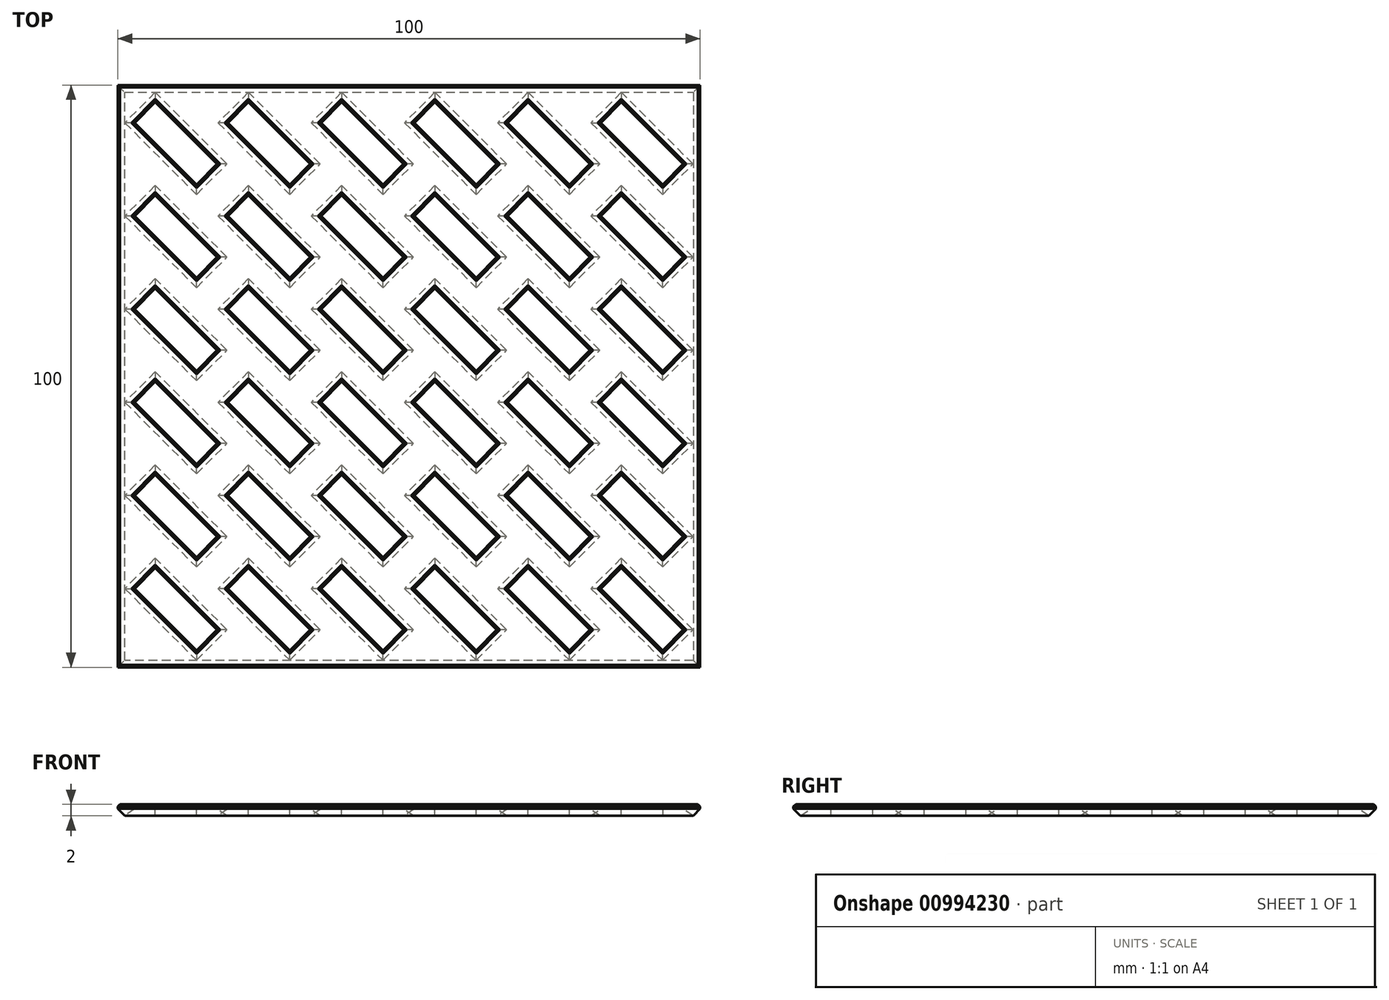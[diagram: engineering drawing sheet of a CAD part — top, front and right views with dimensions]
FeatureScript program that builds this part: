
annotation { "Feature Type Name" : "Feature", "Feature Type Description" : "" }
export const myFeature = defineFeature(function(context is Context, id is Id, definition is map)
    precondition{}
    {
        {
            var Q0;
            Q0=qCreatedBy(makeId("Top.planeOp"),FACE);
            var sketch = newSketch(context, id + "F0", { "sketchPlane" : qUnion([Q0])});
            skLineSegment(sketch, "E0.bottom", {"start": v(-50, -50) * mm, "end": v(50, -50) * mm});
            skLineSegment(sketch, "E0.top", {"start": v(-50, 50) * mm, "end": v(50, 50) * mm});
            skLineSegment(sketch, "E0.left", {"start": v(-50, -50) * mm, "end": v(-50, 50) * mm});
            skLineSegment(sketch, "E0.right", {"start": v(50, -50) * mm, "end": v(50, 50) * mm});
            skLineSegment(sketch, "E1", {"start": v(-50, 50) * mm, "end": v(50, -50) * mm, "construction": true});
            skLineSegment(sketch, "E2", {"start": v(-47.07, -36.46) * mm, "end": v(-36.46, -47.07) * mm});
            skLineSegment(sketch, "E3", {"start": v(-36.46, -47.07) * mm, "end": v(-32.93, -43.54) * mm});
            skLineSegment(sketch, "E4", {"start": v(-32.93, -43.54) * mm, "end": v(-43.54, -32.93) * mm});
            skLineSegment(sketch, "E5", {"start": v(-43.54, -32.93) * mm, "end": v(-47.07, -36.46) * mm});
            skLineSegment(sketch, "E6", {"start": v(-32.93, -43.54) * mm, "end": v(-40, -43.54) * mm, "construction": true});
            skLineSegment(sketch, "E7", {"start": v(-36.46, -47.07) * mm, "end": v(-36.46, -50) * mm, "construction": true});
            skLineSegment(sketch, "E8", {"start": v(-47.07, -36.46) * mm, "end": v(-50, -36.46) * mm, "construction": true});
            skLineSegment(sketch, "E9.0.1.0", {"start": v(-43.54, -16.93) * mm, "end": v(-47.07, -20.46) * mm});
            skLineSegment(sketch, "E9.0.1.1", {"start": v(-47.07, -20.46) * mm, "end": v(-36.46, -31.07) * mm});
            skLineSegment(sketch, "E9.0.1.2", {"start": v(-32.93, -27.54) * mm, "end": v(-43.54, -16.93) * mm});
            skLineSegment(sketch, "E9.0.1.3", {"start": v(-36.46, -31.07) * mm, "end": v(-32.93, -27.54) * mm});
            skLineSegment(sketch, "E9.0.2.0", {"start": v(-43.54, -0.93) * mm, "end": v(-47.07, -4.46) * mm});
            skLineSegment(sketch, "E9.0.2.1", {"start": v(-47.07, -4.46) * mm, "end": v(-36.46, -15.07) * mm});
            skLineSegment(sketch, "E9.0.2.2", {"start": v(-32.93, -11.54) * mm, "end": v(-43.54, -0.93) * mm});
            skLineSegment(sketch, "E9.0.2.3", {"start": v(-36.46, -15.07) * mm, "end": v(-32.93, -11.54) * mm});
            skLineSegment(sketch, "E9.0.3.0", {"start": v(-43.54, 15.07) * mm, "end": v(-47.07, 11.54) * mm});
            skLineSegment(sketch, "E9.0.3.1", {"start": v(-47.07, 11.54) * mm, "end": v(-36.46, 0.93) * mm});
            skLineSegment(sketch, "E9.0.3.2", {"start": v(-32.93, 4.46) * mm, "end": v(-43.54, 15.07) * mm});
            skLineSegment(sketch, "E9.0.3.3", {"start": v(-36.46, 0.93) * mm, "end": v(-32.93, 4.46) * mm});
            skLineSegment(sketch, "E9.0.4.0", {"start": v(-43.54, 31.07) * mm, "end": v(-47.07, 27.54) * mm});
            skLineSegment(sketch, "E9.0.4.1", {"start": v(-47.07, 27.54) * mm, "end": v(-36.46, 16.93) * mm});
            skLineSegment(sketch, "E9.0.4.2", {"start": v(-32.93, 20.46) * mm, "end": v(-43.54, 31.07) * mm});
            skLineSegment(sketch, "E9.0.4.3", {"start": v(-36.46, 16.93) * mm, "end": v(-32.93, 20.46) * mm});
            skLineSegment(sketch, "E9.0.5.0", {"start": v(-43.54, 47.07) * mm, "end": v(-47.07, 43.54) * mm});
            skLineSegment(sketch, "E9.0.5.1", {"start": v(-47.07, 43.54) * mm, "end": v(-36.46, 32.93) * mm});
            skLineSegment(sketch, "E9.0.5.2", {"start": v(-32.93, 36.46) * mm, "end": v(-43.54, 47.07) * mm});
            skLineSegment(sketch, "E9.0.5.3", {"start": v(-36.46, 32.93) * mm, "end": v(-32.93, 36.46) * mm});
            skLineSegment(sketch, "E9.1.0.0", {"start": v(-27.54, -32.93) * mm, "end": v(-31.07, -36.46) * mm});
            skLineSegment(sketch, "E9.1.0.1", {"start": v(-31.07, -36.46) * mm, "end": v(-20.46, -47.07) * mm});
            skLineSegment(sketch, "E9.1.0.2", {"start": v(-16.93, -43.54) * mm, "end": v(-27.54, -32.93) * mm});
            skLineSegment(sketch, "E9.1.0.3", {"start": v(-20.46, -47.07) * mm, "end": v(-16.93, -43.54) * mm});
            skLineSegment(sketch, "E9.1.1.0", {"start": v(-27.54, -16.93) * mm, "end": v(-31.07, -20.46) * mm});
            skLineSegment(sketch, "E9.1.1.1", {"start": v(-31.07, -20.46) * mm, "end": v(-20.46, -31.07) * mm});
            skLineSegment(sketch, "E9.1.1.2", {"start": v(-16.93, -27.54) * mm, "end": v(-27.54, -16.93) * mm});
            skLineSegment(sketch, "E9.1.1.3", {"start": v(-20.46, -31.07) * mm, "end": v(-16.93, -27.54) * mm});
            skLineSegment(sketch, "E9.1.2.0", {"start": v(-27.54, -0.93) * mm, "end": v(-31.07, -4.46) * mm});
            skLineSegment(sketch, "E9.1.2.1", {"start": v(-31.07, -4.46) * mm, "end": v(-20.46, -15.07) * mm});
            skLineSegment(sketch, "E9.1.2.2", {"start": v(-16.93, -11.54) * mm, "end": v(-27.54, -0.93) * mm});
            skLineSegment(sketch, "E9.1.2.3", {"start": v(-20.46, -15.07) * mm, "end": v(-16.93, -11.54) * mm});
            skLineSegment(sketch, "E9.1.3.0", {"start": v(-27.54, 15.07) * mm, "end": v(-31.07, 11.54) * mm});
            skLineSegment(sketch, "E9.1.3.1", {"start": v(-31.07, 11.54) * mm, "end": v(-20.46, 0.93) * mm});
            skLineSegment(sketch, "E9.1.3.2", {"start": v(-16.93, 4.46) * mm, "end": v(-27.54, 15.07) * mm});
            skLineSegment(sketch, "E9.1.3.3", {"start": v(-20.46, 0.93) * mm, "end": v(-16.93, 4.46) * mm});
            skLineSegment(sketch, "E9.1.4.0", {"start": v(-27.54, 31.07) * mm, "end": v(-31.07, 27.54) * mm});
            skLineSegment(sketch, "E9.1.4.1", {"start": v(-31.07, 27.54) * mm, "end": v(-20.46, 16.93) * mm});
            skLineSegment(sketch, "E9.1.4.2", {"start": v(-16.93, 20.46) * mm, "end": v(-27.54, 31.07) * mm});
            skLineSegment(sketch, "E9.1.4.3", {"start": v(-20.46, 16.93) * mm, "end": v(-16.93, 20.46) * mm});
            skLineSegment(sketch, "E9.1.5.0", {"start": v(-27.54, 47.07) * mm, "end": v(-31.07, 43.54) * mm});
            skLineSegment(sketch, "E9.1.5.1", {"start": v(-31.07, 43.54) * mm, "end": v(-20.46, 32.93) * mm});
            skLineSegment(sketch, "E9.1.5.2", {"start": v(-16.93, 36.46) * mm, "end": v(-27.54, 47.07) * mm});
            skLineSegment(sketch, "E9.1.5.3", {"start": v(-20.46, 32.93) * mm, "end": v(-16.93, 36.46) * mm});
            skLineSegment(sketch, "E9.2.0.0", {"start": v(-11.54, -32.93) * mm, "end": v(-15.07, -36.46) * mm});
            skLineSegment(sketch, "E9.2.0.1", {"start": v(-15.07, -36.46) * mm, "end": v(-4.46, -47.07) * mm});
            skLineSegment(sketch, "E9.2.0.2", {"start": v(-0.93, -43.54) * mm, "end": v(-11.54, -32.93) * mm});
            skLineSegment(sketch, "E9.2.0.3", {"start": v(-4.46, -47.07) * mm, "end": v(-0.93, -43.54) * mm});
            skLineSegment(sketch, "E9.2.1.0", {"start": v(-11.54, -16.93) * mm, "end": v(-15.07, -20.46) * mm});
            skLineSegment(sketch, "E9.2.1.1", {"start": v(-15.07, -20.46) * mm, "end": v(-4.46, -31.07) * mm});
            skLineSegment(sketch, "E9.2.1.2", {"start": v(-0.93, -27.54) * mm, "end": v(-11.54, -16.93) * mm});
            skLineSegment(sketch, "E9.2.1.3", {"start": v(-4.46, -31.07) * mm, "end": v(-0.93, -27.54) * mm});
            skLineSegment(sketch, "E9.2.2.0", {"start": v(-11.54, -0.93) * mm, "end": v(-15.07, -4.46) * mm});
            skLineSegment(sketch, "E9.2.2.1", {"start": v(-15.07, -4.46) * mm, "end": v(-4.46, -15.07) * mm});
            skLineSegment(sketch, "E9.2.2.2", {"start": v(-0.93, -11.54) * mm, "end": v(-11.54, -0.93) * mm});
            skLineSegment(sketch, "E9.2.2.3", {"start": v(-4.46, -15.07) * mm, "end": v(-0.93, -11.54) * mm});
            skLineSegment(sketch, "E9.2.3.0", {"start": v(-11.54, 15.07) * mm, "end": v(-15.07, 11.54) * mm});
            skLineSegment(sketch, "E9.2.3.1", {"start": v(-15.07, 11.54) * mm, "end": v(-4.46, 0.93) * mm});
            skLineSegment(sketch, "E9.2.3.2", {"start": v(-0.93, 4.46) * mm, "end": v(-11.54, 15.07) * mm});
            skLineSegment(sketch, "E9.2.3.3", {"start": v(-4.46, 0.93) * mm, "end": v(-0.93, 4.46) * mm});
            skLineSegment(sketch, "E9.2.4.0", {"start": v(-11.54, 31.07) * mm, "end": v(-15.07, 27.54) * mm});
            skLineSegment(sketch, "E9.2.4.1", {"start": v(-15.07, 27.54) * mm, "end": v(-4.46, 16.93) * mm});
            skLineSegment(sketch, "E9.2.4.2", {"start": v(-0.93, 20.46) * mm, "end": v(-11.54, 31.07) * mm});
            skLineSegment(sketch, "E9.2.4.3", {"start": v(-4.46, 16.93) * mm, "end": v(-0.93, 20.46) * mm});
            skLineSegment(sketch, "E9.2.5.0", {"start": v(-11.54, 47.07) * mm, "end": v(-15.07, 43.54) * mm});
            skLineSegment(sketch, "E9.2.5.1", {"start": v(-15.07, 43.54) * mm, "end": v(-4.46, 32.93) * mm});
            skLineSegment(sketch, "E9.2.5.2", {"start": v(-0.93, 36.46) * mm, "end": v(-11.54, 47.07) * mm});
            skLineSegment(sketch, "E9.2.5.3", {"start": v(-4.46, 32.93) * mm, "end": v(-0.93, 36.46) * mm});
            skLineSegment(sketch, "E9.3.0.0", {"start": v(4.46, -32.93) * mm, "end": v(0.93, -36.46) * mm});
            skLineSegment(sketch, "E9.3.0.1", {"start": v(0.93, -36.46) * mm, "end": v(11.54, -47.07) * mm});
            skLineSegment(sketch, "E9.3.0.2", {"start": v(15.07, -43.54) * mm, "end": v(4.46, -32.93) * mm});
            skLineSegment(sketch, "E9.3.0.3", {"start": v(11.54, -47.07) * mm, "end": v(15.07, -43.54) * mm});
            skLineSegment(sketch, "E9.3.1.0", {"start": v(4.46, -16.93) * mm, "end": v(0.93, -20.46) * mm});
            skLineSegment(sketch, "E9.3.1.1", {"start": v(0.93, -20.46) * mm, "end": v(11.54, -31.07) * mm});
            skLineSegment(sketch, "E9.3.1.2", {"start": v(15.07, -27.54) * mm, "end": v(4.46, -16.93) * mm});
            skLineSegment(sketch, "E9.3.1.3", {"start": v(11.54, -31.07) * mm, "end": v(15.07, -27.54) * mm});
            skLineSegment(sketch, "E9.3.2.0", {"start": v(4.46, -0.93) * mm, "end": v(0.93, -4.46) * mm});
            skLineSegment(sketch, "E9.3.2.1", {"start": v(0.93, -4.46) * mm, "end": v(11.54, -15.07) * mm});
            skLineSegment(sketch, "E9.3.2.2", {"start": v(15.07, -11.54) * mm, "end": v(4.46, -0.93) * mm});
            skLineSegment(sketch, "E9.3.2.3", {"start": v(11.54, -15.07) * mm, "end": v(15.07, -11.54) * mm});
            skLineSegment(sketch, "E9.3.3.0", {"start": v(4.46, 15.07) * mm, "end": v(0.93, 11.54) * mm});
            skLineSegment(sketch, "E9.3.3.1", {"start": v(0.93, 11.54) * mm, "end": v(11.54, 0.93) * mm});
            skLineSegment(sketch, "E9.3.3.2", {"start": v(15.07, 4.46) * mm, "end": v(4.46, 15.07) * mm});
            skLineSegment(sketch, "E9.3.3.3", {"start": v(11.54, 0.93) * mm, "end": v(15.07, 4.46) * mm});
            skLineSegment(sketch, "E9.3.4.0", {"start": v(4.46, 31.07) * mm, "end": v(0.93, 27.54) * mm});
            skLineSegment(sketch, "E9.3.4.1", {"start": v(0.93, 27.54) * mm, "end": v(11.54, 16.93) * mm});
            skLineSegment(sketch, "E9.3.4.2", {"start": v(15.07, 20.46) * mm, "end": v(4.46, 31.07) * mm});
            skLineSegment(sketch, "E9.3.4.3", {"start": v(11.54, 16.93) * mm, "end": v(15.07, 20.46) * mm});
            skLineSegment(sketch, "E9.3.5.0", {"start": v(4.46, 47.07) * mm, "end": v(0.93, 43.54) * mm});
            skLineSegment(sketch, "E9.3.5.1", {"start": v(0.93, 43.54) * mm, "end": v(11.54, 32.93) * mm});
            skLineSegment(sketch, "E9.3.5.2", {"start": v(15.07, 36.46) * mm, "end": v(4.46, 47.07) * mm});
            skLineSegment(sketch, "E9.3.5.3", {"start": v(11.54, 32.93) * mm, "end": v(15.07, 36.46) * mm});
            skLineSegment(sketch, "E9.4.0.0", {"start": v(20.46, -32.93) * mm, "end": v(16.93, -36.46) * mm});
            skLineSegment(sketch, "E9.4.0.1", {"start": v(16.93, -36.46) * mm, "end": v(27.54, -47.07) * mm});
            skLineSegment(sketch, "E9.4.0.2", {"start": v(31.07, -43.54) * mm, "end": v(20.46, -32.93) * mm});
            skLineSegment(sketch, "E9.4.0.3", {"start": v(27.54, -47.07) * mm, "end": v(31.07, -43.54) * mm});
            skLineSegment(sketch, "E9.4.1.0", {"start": v(20.46, -16.93) * mm, "end": v(16.93, -20.46) * mm});
            skLineSegment(sketch, "E9.4.1.1", {"start": v(16.93, -20.46) * mm, "end": v(27.54, -31.07) * mm});
            skLineSegment(sketch, "E9.4.1.2", {"start": v(31.07, -27.54) * mm, "end": v(20.46, -16.93) * mm});
            skLineSegment(sketch, "E9.4.1.3", {"start": v(27.54, -31.07) * mm, "end": v(31.07, -27.54) * mm});
            skLineSegment(sketch, "E9.4.2.0", {"start": v(20.46, -0.93) * mm, "end": v(16.93, -4.46) * mm});
            skLineSegment(sketch, "E9.4.2.1", {"start": v(16.93, -4.46) * mm, "end": v(27.54, -15.07) * mm});
            skLineSegment(sketch, "E9.4.2.2", {"start": v(31.07, -11.54) * mm, "end": v(20.46, -0.93) * mm});
            skLineSegment(sketch, "E9.4.2.3", {"start": v(27.54, -15.07) * mm, "end": v(31.07, -11.54) * mm});
            skLineSegment(sketch, "E9.4.3.0", {"start": v(20.46, 15.07) * mm, "end": v(16.93, 11.54) * mm});
            skLineSegment(sketch, "E9.4.3.1", {"start": v(16.93, 11.54) * mm, "end": v(27.54, 0.93) * mm});
            skLineSegment(sketch, "E9.4.3.2", {"start": v(31.07, 4.46) * mm, "end": v(20.46, 15.07) * mm});
            skLineSegment(sketch, "E9.4.3.3", {"start": v(27.54, 0.93) * mm, "end": v(31.07, 4.46) * mm});
            skLineSegment(sketch, "E9.4.4.0", {"start": v(20.46, 31.07) * mm, "end": v(16.93, 27.54) * mm});
            skLineSegment(sketch, "E9.4.4.1", {"start": v(16.93, 27.54) * mm, "end": v(27.54, 16.93) * mm});
            skLineSegment(sketch, "E9.4.4.2", {"start": v(31.07, 20.46) * mm, "end": v(20.46, 31.07) * mm});
            skLineSegment(sketch, "E9.4.4.3", {"start": v(27.54, 16.93) * mm, "end": v(31.07, 20.46) * mm});
            skLineSegment(sketch, "E9.4.5.0", {"start": v(20.46, 47.07) * mm, "end": v(16.93, 43.54) * mm});
            skLineSegment(sketch, "E9.4.5.1", {"start": v(16.93, 43.54) * mm, "end": v(27.54, 32.93) * mm});
            skLineSegment(sketch, "E9.4.5.2", {"start": v(31.07, 36.46) * mm, "end": v(20.46, 47.07) * mm});
            skLineSegment(sketch, "E9.4.5.3", {"start": v(27.54, 32.93) * mm, "end": v(31.07, 36.46) * mm});
            skLineSegment(sketch, "E9.5.0.0", {"start": v(36.46, -32.93) * mm, "end": v(32.93, -36.46) * mm});
            skLineSegment(sketch, "E9.5.0.1", {"start": v(32.93, -36.46) * mm, "end": v(43.54, -47.07) * mm});
            skLineSegment(sketch, "E9.5.0.2", {"start": v(47.07, -43.54) * mm, "end": v(36.46, -32.93) * mm});
            skLineSegment(sketch, "E9.5.0.3", {"start": v(43.54, -47.07) * mm, "end": v(47.07, -43.54) * mm});
            skLineSegment(sketch, "E9.5.1.0", {"start": v(36.46, -16.93) * mm, "end": v(32.93, -20.46) * mm});
            skLineSegment(sketch, "E9.5.1.1", {"start": v(32.93, -20.46) * mm, "end": v(43.54, -31.07) * mm});
            skLineSegment(sketch, "E9.5.1.2", {"start": v(47.07, -27.54) * mm, "end": v(36.46, -16.93) * mm});
            skLineSegment(sketch, "E9.5.1.3", {"start": v(43.54, -31.07) * mm, "end": v(47.07, -27.54) * mm});
            skLineSegment(sketch, "E9.5.2.0", {"start": v(36.46, -0.93) * mm, "end": v(32.93, -4.46) * mm});
            skLineSegment(sketch, "E9.5.2.1", {"start": v(32.93, -4.46) * mm, "end": v(43.54, -15.07) * mm});
            skLineSegment(sketch, "E9.5.2.2", {"start": v(47.07, -11.54) * mm, "end": v(36.46, -0.93) * mm});
            skLineSegment(sketch, "E9.5.2.3", {"start": v(43.54, -15.07) * mm, "end": v(47.07, -11.54) * mm});
            skLineSegment(sketch, "E9.5.3.0", {"start": v(36.46, 15.07) * mm, "end": v(32.93, 11.54) * mm});
            skLineSegment(sketch, "E9.5.3.1", {"start": v(32.93, 11.54) * mm, "end": v(43.54, 0.93) * mm});
            skLineSegment(sketch, "E9.5.3.2", {"start": v(47.07, 4.46) * mm, "end": v(36.46, 15.07) * mm});
            skLineSegment(sketch, "E9.5.3.3", {"start": v(43.54, 0.93) * mm, "end": v(47.07, 4.46) * mm});
            skLineSegment(sketch, "E9.5.4.0", {"start": v(36.46, 31.07) * mm, "end": v(32.93, 27.54) * mm});
            skLineSegment(sketch, "E9.5.4.1", {"start": v(32.93, 27.54) * mm, "end": v(43.54, 16.93) * mm});
            skLineSegment(sketch, "E9.5.4.2", {"start": v(47.07, 20.46) * mm, "end": v(36.46, 31.07) * mm});
            skLineSegment(sketch, "E9.5.4.3", {"start": v(43.54, 16.93) * mm, "end": v(47.07, 20.46) * mm});
            skLineSegment(sketch, "E9.5.5.0", {"start": v(36.46, 47.07) * mm, "end": v(32.93, 43.54) * mm});
            skLineSegment(sketch, "E9.5.5.1", {"start": v(32.93, 43.54) * mm, "end": v(43.54, 32.93) * mm});
            skLineSegment(sketch, "E9.5.5.2", {"start": v(47.07, 36.46) * mm, "end": v(36.46, 47.07) * mm});
            skLineSegment(sketch, "E9.5.5.3", {"start": v(43.54, 32.93) * mm, "end": v(47.07, 36.46) * mm});
            skLineSegment(sketch, "E9.direction1", {"start": v(-47.07, -36.46) * mm, "end": v(-31.07, -36.46) * mm, "construction": true});
            skLineSegment(sketch, "E9.direction2", {"start": v(-47.07, -36.46) * mm, "end": v(-47.07, -20.46) * mm, "construction": true});
            skLineSegment(sketch, "E10", {"start": v(36.46, 47.07) * mm, "end": v(36.46, 50) * mm, "construction": true});
            skLineSegment(sketch, "E11", {"start": v(47.07, 36.46) * mm, "end": v(50, 36.46) * mm, "construction": true});
            skSolve(sketch);
        }
        {
            var Q0;
            Q0=makeQuery(id+"F0.imprint","IMPRINT",FACE,{"disambiguationData":[TD([[makeQuery(id+"F0.imprint","IMPRINT",EDGE,{"derivedFrom":sQuery(id+"F0.wireOp",EDGE,"E0.bottom")}),1.0]])]});
            extrude(context, id + "F1", {"entities" : qUnion([Q0]), "depth" : 2 * mm, "offsetDistance" : 25 * mm});
        }
        {
            var Q0;
            Q0=makeQuery(id+"F1.opExtrude","CAP_FACE",FACE,{"disambiguationData":[OSD([sQuery(id+"F0.wireOp",EDGE,"E0.bottom"),sQuery(id+"F0.wireOp",EDGE,"E0.top"),sQuery(id+"F0.wireOp",EDGE,"E0.left"),sQuery(id+"F0.wireOp",EDGE,"E0.right"),sQuery(id+"F0.wireOp",EDGE,"E2"),sQuery(id+"F0.wireOp",EDGE,"E3"),sQuery(id+"F0.wireOp",EDGE,"E4"),sQuery(id+"F0.wireOp",EDGE,"E5"),sQuery(id+"F0.wireOp",EDGE,"E9.0.1.0"),sQuery(id+"F0.wireOp",EDGE,"E9.0.1.1"),sQuery(id+"F0.wireOp",EDGE,"E9.0.1.2"),sQuery(id+"F0.wireOp",EDGE,"E9.0.1.3"),sQuery(id+"F0.wireOp",EDGE,"E9.0.2.0"),sQuery(id+"F0.wireOp",EDGE,"E9.0.2.1"),sQuery(id+"F0.wireOp",EDGE,"E9.0.2.2"),sQuery(id+"F0.wireOp",EDGE,"E9.0.2.3"),sQuery(id+"F0.wireOp",EDGE,"E9.0.3.0"),sQuery(id+"F0.wireOp",EDGE,"E9.0.3.1"),sQuery(id+"F0.wireOp",EDGE,"E9.0.3.2"),sQuery(id+"F0.wireOp",EDGE,"E9.0.3.3"),sQuery(id+"F0.wireOp",EDGE,"E9.0.4.0"),sQuery(id+"F0.wireOp",EDGE,"E9.0.4.1"),sQuery(id+"F0.wireOp",EDGE,"E9.0.4.2"),sQuery(id+"F0.wireOp",EDGE,"E9.0.4.3"),sQuery(id+"F0.wireOp",EDGE,"E9.0.5.0"),sQuery(id+"F0.wireOp",EDGE,"E9.0.5.1"),sQuery(id+"F0.wireOp",EDGE,"E9.0.5.2"),sQuery(id+"F0.wireOp",EDGE,"E9.0.5.3"),sQuery(id+"F0.wireOp",EDGE,"E9.1.0.0"),sQuery(id+"F0.wireOp",EDGE,"E9.1.0.1"),sQuery(id+"F0.wireOp",EDGE,"E9.1.0.2"),sQuery(id+"F0.wireOp",EDGE,"E9.1.0.3"),sQuery(id+"F0.wireOp",EDGE,"E9.1.1.0"),sQuery(id+"F0.wireOp",EDGE,"E9.1.1.1"),sQuery(id+"F0.wireOp",EDGE,"E9.1.1.2"),sQuery(id+"F0.wireOp",EDGE,"E9.1.1.3"),sQuery(id+"F0.wireOp",EDGE,"E9.1.2.0"),sQuery(id+"F0.wireOp",EDGE,"E9.1.2.1"),sQuery(id+"F0.wireOp",EDGE,"E9.1.2.2"),sQuery(id+"F0.wireOp",EDGE,"E9.1.2.3"),sQuery(id+"F0.wireOp",EDGE,"E9.1.3.0"),sQuery(id+"F0.wireOp",EDGE,"E9.1.3.1"),sQuery(id+"F0.wireOp",EDGE,"E9.1.3.2"),sQuery(id+"F0.wireOp",EDGE,"E9.1.3.3"),sQuery(id+"F0.wireOp",EDGE,"E9.1.4.0"),sQuery(id+"F0.wireOp",EDGE,"E9.1.4.1"),sQuery(id+"F0.wireOp",EDGE,"E9.1.4.2"),sQuery(id+"F0.wireOp",EDGE,"E9.1.4.3"),sQuery(id+"F0.wireOp",EDGE,"E9.1.5.0"),sQuery(id+"F0.wireOp",EDGE,"E9.1.5.1"),sQuery(id+"F0.wireOp",EDGE,"E9.1.5.2"),sQuery(id+"F0.wireOp",EDGE,"E9.1.5.3"),sQuery(id+"F0.wireOp",EDGE,"E9.2.0.0"),sQuery(id+"F0.wireOp",EDGE,"E9.2.0.1"),sQuery(id+"F0.wireOp",EDGE,"E9.2.0.2"),sQuery(id+"F0.wireOp",EDGE,"E9.2.0.3"),sQuery(id+"F0.wireOp",EDGE,"E9.2.1.0"),sQuery(id+"F0.wireOp",EDGE,"E9.2.1.1"),sQuery(id+"F0.wireOp",EDGE,"E9.2.1.2"),sQuery(id+"F0.wireOp",EDGE,"E9.2.1.3"),sQuery(id+"F0.wireOp",EDGE,"E9.2.2.0"),sQuery(id+"F0.wireOp",EDGE,"E9.2.2.1"),sQuery(id+"F0.wireOp",EDGE,"E9.2.2.2"),sQuery(id+"F0.wireOp",EDGE,"E9.2.2.3"),sQuery(id+"F0.wireOp",EDGE,"E9.2.3.0"),sQuery(id+"F0.wireOp",EDGE,"E9.2.3.1"),sQuery(id+"F0.wireOp",EDGE,"E9.2.3.2"),sQuery(id+"F0.wireOp",EDGE,"E9.2.3.3"),sQuery(id+"F0.wireOp",EDGE,"E9.2.4.0"),sQuery(id+"F0.wireOp",EDGE,"E9.2.4.1"),sQuery(id+"F0.wireOp",EDGE,"E9.2.4.2"),sQuery(id+"F0.wireOp",EDGE,"E9.2.4.3"),sQuery(id+"F0.wireOp",EDGE,"E9.2.5.0"),sQuery(id+"F0.wireOp",EDGE,"E9.2.5.1"),sQuery(id+"F0.wireOp",EDGE,"E9.2.5.2"),sQuery(id+"F0.wireOp",EDGE,"E9.2.5.3"),sQuery(id+"F0.wireOp",EDGE,"E9.3.0.0"),sQuery(id+"F0.wireOp",EDGE,"E9.3.0.1"),sQuery(id+"F0.wireOp",EDGE,"E9.3.0.2"),sQuery(id+"F0.wireOp",EDGE,"E9.3.0.3"),sQuery(id+"F0.wireOp",EDGE,"E9.3.1.0"),sQuery(id+"F0.wireOp",EDGE,"E9.3.1.1"),sQuery(id+"F0.wireOp",EDGE,"E9.3.1.2"),sQuery(id+"F0.wireOp",EDGE,"E9.3.1.3"),sQuery(id+"F0.wireOp",EDGE,"E9.3.2.0"),sQuery(id+"F0.wireOp",EDGE,"E9.3.2.1"),sQuery(id+"F0.wireOp",EDGE,"E9.3.2.2"),sQuery(id+"F0.wireOp",EDGE,"E9.3.2.3"),sQuery(id+"F0.wireOp",EDGE,"E9.3.3.0"),sQuery(id+"F0.wireOp",EDGE,"E9.3.3.1"),sQuery(id+"F0.wireOp",EDGE,"E9.3.3.2"),sQuery(id+"F0.wireOp",EDGE,"E9.3.3.3"),sQuery(id+"F0.wireOp",EDGE,"E9.3.4.0"),sQuery(id+"F0.wireOp",EDGE,"E9.3.4.1"),sQuery(id+"F0.wireOp",EDGE,"E9.3.4.2"),sQuery(id+"F0.wireOp",EDGE,"E9.3.4.3"),sQuery(id+"F0.wireOp",EDGE,"E9.3.5.0"),sQuery(id+"F0.wireOp",EDGE,"E9.3.5.1"),sQuery(id+"F0.wireOp",EDGE,"E9.3.5.2"),sQuery(id+"F0.wireOp",EDGE,"E9.3.5.3"),sQuery(id+"F0.wireOp",EDGE,"E9.4.0.0"),sQuery(id+"F0.wireOp",EDGE,"E9.4.0.1"),sQuery(id+"F0.wireOp",EDGE,"E9.4.0.2"),sQuery(id+"F0.wireOp",EDGE,"E9.4.0.3"),sQuery(id+"F0.wireOp",EDGE,"E9.4.1.0"),sQuery(id+"F0.wireOp",EDGE,"E9.4.1.1"),sQuery(id+"F0.wireOp",EDGE,"E9.4.1.2"),sQuery(id+"F0.wireOp",EDGE,"E9.4.1.3"),sQuery(id+"F0.wireOp",EDGE,"E9.4.2.0"),sQuery(id+"F0.wireOp",EDGE,"E9.4.2.1"),sQuery(id+"F0.wireOp",EDGE,"E9.4.2.2"),sQuery(id+"F0.wireOp",EDGE,"E9.4.2.3"),sQuery(id+"F0.wireOp",EDGE,"E9.4.3.0"),sQuery(id+"F0.wireOp",EDGE,"E9.4.3.1"),sQuery(id+"F0.wireOp",EDGE,"E9.4.3.2"),sQuery(id+"F0.wireOp",EDGE,"E9.4.3.3"),sQuery(id+"F0.wireOp",EDGE,"E9.4.4.0"),sQuery(id+"F0.wireOp",EDGE,"E9.4.4.1"),sQuery(id+"F0.wireOp",EDGE,"E9.4.4.2"),sQuery(id+"F0.wireOp",EDGE,"E9.4.4.3"),sQuery(id+"F0.wireOp",EDGE,"E9.4.5.0"),sQuery(id+"F0.wireOp",EDGE,"E9.4.5.1"),sQuery(id+"F0.wireOp",EDGE,"E9.4.5.2"),sQuery(id+"F0.wireOp",EDGE,"E9.4.5.3"),sQuery(id+"F0.wireOp",EDGE,"E9.5.0.0"),sQuery(id+"F0.wireOp",EDGE,"E9.5.0.1"),sQuery(id+"F0.wireOp",EDGE,"E9.5.0.2"),sQuery(id+"F0.wireOp",EDGE,"E9.5.0.3"),sQuery(id+"F0.wireOp",EDGE,"E9.5.1.0"),sQuery(id+"F0.wireOp",EDGE,"E9.5.1.1"),sQuery(id+"F0.wireOp",EDGE,"E9.5.1.2"),sQuery(id+"F0.wireOp",EDGE,"E9.5.1.3"),sQuery(id+"F0.wireOp",EDGE,"E9.5.2.0"),sQuery(id+"F0.wireOp",EDGE,"E9.5.2.1"),sQuery(id+"F0.wireOp",EDGE,"E9.5.2.2"),sQuery(id+"F0.wireOp",EDGE,"E9.5.2.3"),sQuery(id+"F0.wireOp",EDGE,"E9.5.3.0"),sQuery(id+"F0.wireOp",EDGE,"E9.5.3.1"),sQuery(id+"F0.wireOp",EDGE,"E9.5.3.2"),sQuery(id+"F0.wireOp",EDGE,"E9.5.3.3"),sQuery(id+"F0.wireOp",EDGE,"E9.5.4.0"),sQuery(id+"F0.wireOp",EDGE,"E9.5.4.1"),sQuery(id+"F0.wireOp",EDGE,"E9.5.4.2"),sQuery(id+"F0.wireOp",EDGE,"E9.5.4.3"),sQuery(id+"F0.wireOp",EDGE,"E9.5.5.0"),sQuery(id+"F0.wireOp",EDGE,"E9.5.5.1"),sQuery(id+"F0.wireOp",EDGE,"E9.5.5.2"),sQuery(id+"F0.wireOp",EDGE,"E9.5.5.3")])],"isStart":false});
            chamfer(context, id + "F2", {"entities" : qUnion([Q0]), "width" : .4 * mm, "tangentPropagation" : true});
        }
        {
            var Q0;
            Q0=makeQuery(id+"F1.opExtrude","CAP_FACE",FACE,{"disambiguationData":[OSD([sQuery(id+"F0.wireOp",EDGE,"E0.bottom"),sQuery(id+"F0.wireOp",EDGE,"E0.top"),sQuery(id+"F0.wireOp",EDGE,"E0.left"),sQuery(id+"F0.wireOp",EDGE,"E0.right"),sQuery(id+"F0.wireOp",EDGE,"E2"),sQuery(id+"F0.wireOp",EDGE,"E3"),sQuery(id+"F0.wireOp",EDGE,"E4"),sQuery(id+"F0.wireOp",EDGE,"E5"),sQuery(id+"F0.wireOp",EDGE,"E9.0.1.0"),sQuery(id+"F0.wireOp",EDGE,"E9.0.1.1"),sQuery(id+"F0.wireOp",EDGE,"E9.0.1.2"),sQuery(id+"F0.wireOp",EDGE,"E9.0.1.3"),sQuery(id+"F0.wireOp",EDGE,"E9.0.2.0"),sQuery(id+"F0.wireOp",EDGE,"E9.0.2.1"),sQuery(id+"F0.wireOp",EDGE,"E9.0.2.2"),sQuery(id+"F0.wireOp",EDGE,"E9.0.2.3"),sQuery(id+"F0.wireOp",EDGE,"E9.0.3.0"),sQuery(id+"F0.wireOp",EDGE,"E9.0.3.1"),sQuery(id+"F0.wireOp",EDGE,"E9.0.3.2"),sQuery(id+"F0.wireOp",EDGE,"E9.0.3.3"),sQuery(id+"F0.wireOp",EDGE,"E9.0.4.0"),sQuery(id+"F0.wireOp",EDGE,"E9.0.4.1"),sQuery(id+"F0.wireOp",EDGE,"E9.0.4.2"),sQuery(id+"F0.wireOp",EDGE,"E9.0.4.3"),sQuery(id+"F0.wireOp",EDGE,"E9.0.5.0"),sQuery(id+"F0.wireOp",EDGE,"E9.0.5.1"),sQuery(id+"F0.wireOp",EDGE,"E9.0.5.2"),sQuery(id+"F0.wireOp",EDGE,"E9.0.5.3"),sQuery(id+"F0.wireOp",EDGE,"E9.1.0.0"),sQuery(id+"F0.wireOp",EDGE,"E9.1.0.1"),sQuery(id+"F0.wireOp",EDGE,"E9.1.0.2"),sQuery(id+"F0.wireOp",EDGE,"E9.1.0.3"),sQuery(id+"F0.wireOp",EDGE,"E9.1.1.0"),sQuery(id+"F0.wireOp",EDGE,"E9.1.1.1"),sQuery(id+"F0.wireOp",EDGE,"E9.1.1.2"),sQuery(id+"F0.wireOp",EDGE,"E9.1.1.3"),sQuery(id+"F0.wireOp",EDGE,"E9.1.2.0"),sQuery(id+"F0.wireOp",EDGE,"E9.1.2.1"),sQuery(id+"F0.wireOp",EDGE,"E9.1.2.2"),sQuery(id+"F0.wireOp",EDGE,"E9.1.2.3"),sQuery(id+"F0.wireOp",EDGE,"E9.1.3.0"),sQuery(id+"F0.wireOp",EDGE,"E9.1.3.1"),sQuery(id+"F0.wireOp",EDGE,"E9.1.3.2"),sQuery(id+"F0.wireOp",EDGE,"E9.1.3.3"),sQuery(id+"F0.wireOp",EDGE,"E9.1.4.0"),sQuery(id+"F0.wireOp",EDGE,"E9.1.4.1"),sQuery(id+"F0.wireOp",EDGE,"E9.1.4.2"),sQuery(id+"F0.wireOp",EDGE,"E9.1.4.3"),sQuery(id+"F0.wireOp",EDGE,"E9.1.5.0"),sQuery(id+"F0.wireOp",EDGE,"E9.1.5.1"),sQuery(id+"F0.wireOp",EDGE,"E9.1.5.2"),sQuery(id+"F0.wireOp",EDGE,"E9.1.5.3"),sQuery(id+"F0.wireOp",EDGE,"E9.2.0.0"),sQuery(id+"F0.wireOp",EDGE,"E9.2.0.1"),sQuery(id+"F0.wireOp",EDGE,"E9.2.0.2"),sQuery(id+"F0.wireOp",EDGE,"E9.2.0.3"),sQuery(id+"F0.wireOp",EDGE,"E9.2.1.0"),sQuery(id+"F0.wireOp",EDGE,"E9.2.1.1"),sQuery(id+"F0.wireOp",EDGE,"E9.2.1.2"),sQuery(id+"F0.wireOp",EDGE,"E9.2.1.3"),sQuery(id+"F0.wireOp",EDGE,"E9.2.2.0"),sQuery(id+"F0.wireOp",EDGE,"E9.2.2.1"),sQuery(id+"F0.wireOp",EDGE,"E9.2.2.2"),sQuery(id+"F0.wireOp",EDGE,"E9.2.2.3"),sQuery(id+"F0.wireOp",EDGE,"E9.2.3.0"),sQuery(id+"F0.wireOp",EDGE,"E9.2.3.1"),sQuery(id+"F0.wireOp",EDGE,"E9.2.3.2"),sQuery(id+"F0.wireOp",EDGE,"E9.2.3.3"),sQuery(id+"F0.wireOp",EDGE,"E9.2.4.0"),sQuery(id+"F0.wireOp",EDGE,"E9.2.4.1"),sQuery(id+"F0.wireOp",EDGE,"E9.2.4.2"),sQuery(id+"F0.wireOp",EDGE,"E9.2.4.3"),sQuery(id+"F0.wireOp",EDGE,"E9.2.5.0"),sQuery(id+"F0.wireOp",EDGE,"E9.2.5.1"),sQuery(id+"F0.wireOp",EDGE,"E9.2.5.2"),sQuery(id+"F0.wireOp",EDGE,"E9.2.5.3"),sQuery(id+"F0.wireOp",EDGE,"E9.3.0.0"),sQuery(id+"F0.wireOp",EDGE,"E9.3.0.1"),sQuery(id+"F0.wireOp",EDGE,"E9.3.0.2"),sQuery(id+"F0.wireOp",EDGE,"E9.3.0.3"),sQuery(id+"F0.wireOp",EDGE,"E9.3.1.0"),sQuery(id+"F0.wireOp",EDGE,"E9.3.1.1"),sQuery(id+"F0.wireOp",EDGE,"E9.3.1.2"),sQuery(id+"F0.wireOp",EDGE,"E9.3.1.3"),sQuery(id+"F0.wireOp",EDGE,"E9.3.2.0"),sQuery(id+"F0.wireOp",EDGE,"E9.3.2.1"),sQuery(id+"F0.wireOp",EDGE,"E9.3.2.2"),sQuery(id+"F0.wireOp",EDGE,"E9.3.2.3"),sQuery(id+"F0.wireOp",EDGE,"E9.3.3.0"),sQuery(id+"F0.wireOp",EDGE,"E9.3.3.1"),sQuery(id+"F0.wireOp",EDGE,"E9.3.3.2"),sQuery(id+"F0.wireOp",EDGE,"E9.3.3.3"),sQuery(id+"F0.wireOp",EDGE,"E9.3.4.0"),sQuery(id+"F0.wireOp",EDGE,"E9.3.4.1"),sQuery(id+"F0.wireOp",EDGE,"E9.3.4.2"),sQuery(id+"F0.wireOp",EDGE,"E9.3.4.3"),sQuery(id+"F0.wireOp",EDGE,"E9.3.5.0"),sQuery(id+"F0.wireOp",EDGE,"E9.3.5.1"),sQuery(id+"F0.wireOp",EDGE,"E9.3.5.2"),sQuery(id+"F0.wireOp",EDGE,"E9.3.5.3"),sQuery(id+"F0.wireOp",EDGE,"E9.4.0.0"),sQuery(id+"F0.wireOp",EDGE,"E9.4.0.1"),sQuery(id+"F0.wireOp",EDGE,"E9.4.0.2"),sQuery(id+"F0.wireOp",EDGE,"E9.4.0.3"),sQuery(id+"F0.wireOp",EDGE,"E9.4.1.0"),sQuery(id+"F0.wireOp",EDGE,"E9.4.1.1"),sQuery(id+"F0.wireOp",EDGE,"E9.4.1.2"),sQuery(id+"F0.wireOp",EDGE,"E9.4.1.3"),sQuery(id+"F0.wireOp",EDGE,"E9.4.2.0"),sQuery(id+"F0.wireOp",EDGE,"E9.4.2.1"),sQuery(id+"F0.wireOp",EDGE,"E9.4.2.2"),sQuery(id+"F0.wireOp",EDGE,"E9.4.2.3"),sQuery(id+"F0.wireOp",EDGE,"E9.4.3.0"),sQuery(id+"F0.wireOp",EDGE,"E9.4.3.1"),sQuery(id+"F0.wireOp",EDGE,"E9.4.3.2"),sQuery(id+"F0.wireOp",EDGE,"E9.4.3.3"),sQuery(id+"F0.wireOp",EDGE,"E9.4.4.0"),sQuery(id+"F0.wireOp",EDGE,"E9.4.4.1"),sQuery(id+"F0.wireOp",EDGE,"E9.4.4.2"),sQuery(id+"F0.wireOp",EDGE,"E9.4.4.3"),sQuery(id+"F0.wireOp",EDGE,"E9.4.5.0"),sQuery(id+"F0.wireOp",EDGE,"E9.4.5.1"),sQuery(id+"F0.wireOp",EDGE,"E9.4.5.2"),sQuery(id+"F0.wireOp",EDGE,"E9.4.5.3"),sQuery(id+"F0.wireOp",EDGE,"E9.5.0.0"),sQuery(id+"F0.wireOp",EDGE,"E9.5.0.1"),sQuery(id+"F0.wireOp",EDGE,"E9.5.0.2"),sQuery(id+"F0.wireOp",EDGE,"E9.5.0.3"),sQuery(id+"F0.wireOp",EDGE,"E9.5.1.0"),sQuery(id+"F0.wireOp",EDGE,"E9.5.1.1"),sQuery(id+"F0.wireOp",EDGE,"E9.5.1.2"),sQuery(id+"F0.wireOp",EDGE,"E9.5.1.3"),sQuery(id+"F0.wireOp",EDGE,"E9.5.2.0"),sQuery(id+"F0.wireOp",EDGE,"E9.5.2.1"),sQuery(id+"F0.wireOp",EDGE,"E9.5.2.2"),sQuery(id+"F0.wireOp",EDGE,"E9.5.2.3"),sQuery(id+"F0.wireOp",EDGE,"E9.5.3.0"),sQuery(id+"F0.wireOp",EDGE,"E9.5.3.1"),sQuery(id+"F0.wireOp",EDGE,"E9.5.3.2"),sQuery(id+"F0.wireOp",EDGE,"E9.5.3.3"),sQuery(id+"F0.wireOp",EDGE,"E9.5.4.0"),sQuery(id+"F0.wireOp",EDGE,"E9.5.4.1"),sQuery(id+"F0.wireOp",EDGE,"E9.5.4.2"),sQuery(id+"F0.wireOp",EDGE,"E9.5.4.3"),sQuery(id+"F0.wireOp",EDGE,"E9.5.5.0"),sQuery(id+"F0.wireOp",EDGE,"E9.5.5.1"),sQuery(id+"F0.wireOp",EDGE,"E9.5.5.2"),sQuery(id+"F0.wireOp",EDGE,"E9.5.5.3")])],"isStart":true});
            chamfer(context, id + "F3", {"entities" : qUnion([Q0]), "width" : 1.2 * mm, "tangentPropagation" : true});
        }
    });
